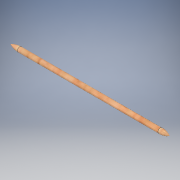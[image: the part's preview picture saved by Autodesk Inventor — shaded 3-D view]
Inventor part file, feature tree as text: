
AUTODESK INVENTOR PART (.ipt)
format: ipt  version: 2016 (Build 200138000, 138)  size: 105,472 bytes
history: native  units: in
note: dims shown in document units (in); Inventor stores cm internally (conversion verified against a paired STEP export)
features: sketch x2, extrude x1, revolve x1
ambient origin geometry x8: Origin, YZ Plane, XZ Plane, XY Plane, X Axis, Y Axis, Z Axis, Center Point
bodies: Solid1 (feature_tree)
feature tree (4):
  extrude  "Extrusion1"  Depth=3.0in TaperAngle=0.0deg
  revolve  "Revolution1"  [1 undecoded]
  sketch  "Sketch1"  dims[d0=0.1in d1=3.0in d2=0.0in]
  sketch  "Sketch2"  dims[d3=0.2in d4=0.2in d5=90.0deg]
note: 1 required parameter value undecoded (feature->parameter linkage not recoverable at this tier; creation-order binding heuristic only, values carry confidence <= 0.55)
